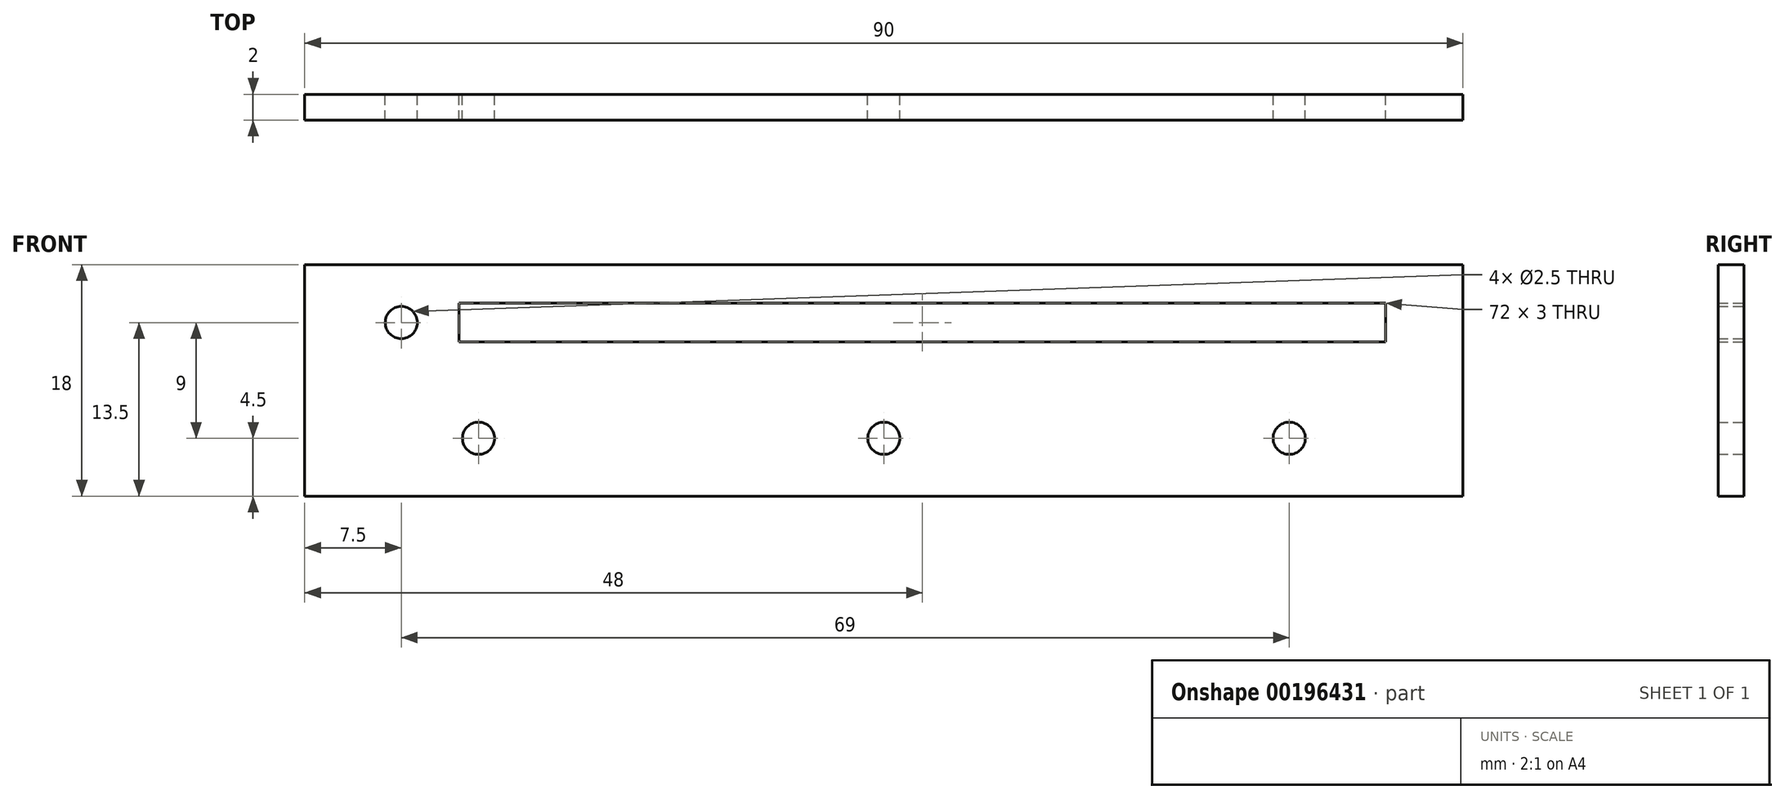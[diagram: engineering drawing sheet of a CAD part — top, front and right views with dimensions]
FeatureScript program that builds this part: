
annotation { "Feature Type Name" : "Feature", "Feature Type Description" : "" }
export const myFeature = defineFeature(function(context is Context, id is Id, definition is map)
    precondition{}
    {
        {
            var Q0;
            Q0=qCreatedBy(makeId("Front.planeOp"),FACE);
            var sketch = newSketch(context, id + "F0", { "sketchPlane" : qUnion([Q0])});
            skLineSegment(sketch, "E0.bottom", {"start": v(42, 4.5) * mm, "end": v(-42, 4.5) * mm});
            skLineSegment(sketch, "E0.top", {"start": v(42, -4.5) * mm, "end": v(-42, -4.5) * mm});
            skLineSegment(sketch, "E0.left", {"start": v(42, 4.5) * mm, "end": v(42, -4.5) * mm});
            skLineSegment(sketch, "E0.right", {"start": v(-42, 4.5) * mm, "end": v(-42, -4.5) * mm});
            skPoint(sketch, "E0.middle", {"position": v(0, 0) * mm});
            skLineSegment(sketch, "E1.bottom", {"start": v(39, 1.5) * mm, "end": v(-33, 1.5) * mm});
            skLineSegment(sketch, "E1.top", {"start": v(39, -1.5) * mm, "end": v(-33, -1.5) * mm});
            skLineSegment(sketch, "E1.left", {"start": v(39, 1.5) * mm, "end": v(39, -1.5) * mm});
            skLineSegment(sketch, "E1.right", {"start": v(-33, 1.5) * mm, "end": v(-33, -1.5) * mm});
            skCircle(sketch, "E2", {"center": v(-37.5, 0) * mm, "radius": 1.25 * mm});
            skLineSegment(sketch, "E3.bottom", {"start": v(-42, -4.5) * mm, "end": v(42, -4.5) * mm});
            skLineSegment(sketch, "E3.top", {"start": v(-42, -13.5) * mm, "end": v(42, -13.5) * mm});
            skLineSegment(sketch, "E3.left", {"start": v(-42, -4.5) * mm, "end": v(-42, -13.5) * mm});
            skLineSegment(sketch, "E3.right", {"start": v(42, -4.5) * mm, "end": v(42, -13.5) * mm});
            skCircle(sketch, "E4", {"center": v(-31.5, -9) * mm, "radius": 1.25 * mm});
            skCircle(sketch, "E5", {"center": v(0, -9) * mm, "radius": 1.25 * mm});
            skCircle(sketch, "E6", {"center": v(31.5, -9) * mm, "radius": 1.25 * mm});
            skLineSegment(sketch, "E7.bottom", {"start": v(-42, 4.5) * mm, "end": v(-45, 4.5) * mm});
            skLineSegment(sketch, "E7.top", {"start": v(-42, -13.5) * mm, "end": v(-45, -13.5) * mm});
            skLineSegment(sketch, "E7.left", {"start": v(-42, 4.5) * mm, "end": v(-42, -13.5) * mm});
            skLineSegment(sketch, "E7.right", {"start": v(-45, 4.5) * mm, "end": v(-45, -13.5) * mm});
            skLineSegment(sketch, "E8.bottom", {"start": v(42, 4.5) * mm, "end": v(45, 4.5) * mm});
            skLineSegment(sketch, "E8.top", {"start": v(42, -13.5) * mm, "end": v(45, -13.5) * mm});
            skLineSegment(sketch, "E8.left", {"start": v(42, 4.5) * mm, "end": v(42, -13.5) * mm});
            skLineSegment(sketch, "E8.right", {"start": v(45, 4.5) * mm, "end": v(45, -13.5) * mm});
            skLineSegment(sketch, "E9", {"start": v(-37.5, 0) * mm, "end": v(-37.5, -13.5) * mm, "construction": true});
            skLineSegment(sketch, "E10", {"start": v(-37.5, -13.5) * mm, "end": v(-37.5, -9) * mm, "construction": true});
            skLineSegment(sketch, "E11", {"start": v(-37.5, -9) * mm, "end": v(-31.5, -9) * mm, "construction": true});
            skSolve(sketch);
        }
        {
            var Q0;
            Q0=qSketchRegion(id+"F0",true);
            extrude(context, id + "F1", {"entities" : qUnion([Q0]), "depth" : 2 * mm});
        }
    });
